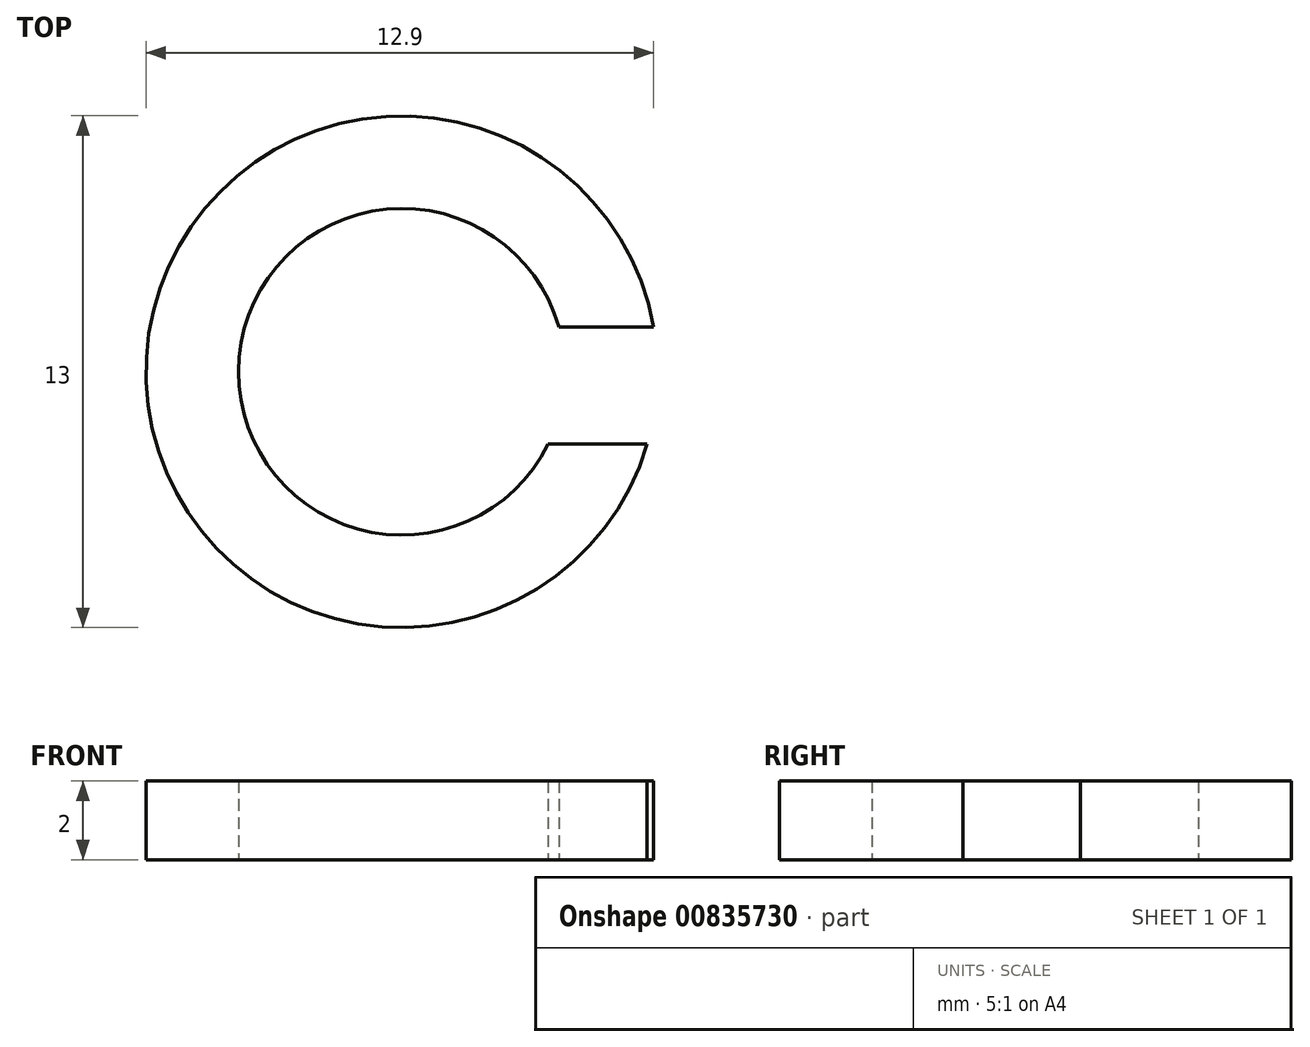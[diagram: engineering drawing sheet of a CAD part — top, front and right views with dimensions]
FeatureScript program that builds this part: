
annotation { "Feature Type Name" : "Feature", "Feature Type Description" : "" }
export const myFeature = defineFeature(function(context is Context, id is Id, definition is map)
    precondition{}
    {
        {
            var Q0;
            Q0=qCreatedBy(makeId("Top.planeOp"),FACE);
            var sketch = newSketch(context, id + "F0", { "sketchPlane" : qUnion([Q0])});
            skCircle(sketch, "E0", {"center": v(-70.8, -48.87) * mm, "radius": 4.15 * mm});
            skCircle(sketch, "E1", {"center": v(-70.8, -48.87) * mm, "radius": 6.5 * mm});
            skLineSegment(sketch, "E2.bottom", {"start": v(-67.78, -47.73) * mm, "end": v(-62.89, -47.73) * mm});
            skLineSegment(sketch, "E2.top", {"start": v(-67.78, -50.71) * mm, "end": v(-62.89, -50.71) * mm});
            skSolve(sketch);
        }
        {
            var Q0;
            Q0=qSketchRegion(id+"F0",true);
            extrude(context, id + "F1", {"entities" : qUnion([Q0]), "depth" : 2 * mm});
        }
        {
            var Q0;
            {var subQ0=sQuery(id+"F0.wireOp",EDGE,"E2.bottom");var subQ1=sQuery(id+"F0.wireOp",EDGE,"E0");var subQ2=makeQuery(id+"F0.imprint","INTERSECT",VERTEX,{"derivedFrom":[subQ1,subQ0]});Q0=makeQuery(id+"F0.imprint","IMPRINT",FACE,{"disambiguationData":[TD([[makeQuery(id+"F0.imprint","IMPRINT",EDGE,{"disambiguationData":[TD([[subQ2,1.0]])],"derivedFrom":subQ1}),-1.0]])]});}
            extrude(context, id + "F2", {"entities" : qUnion([Q0]), "operationType" : NewBodyOperationType.REMOVE, "depth" : 25 * mm});
        }
    });
